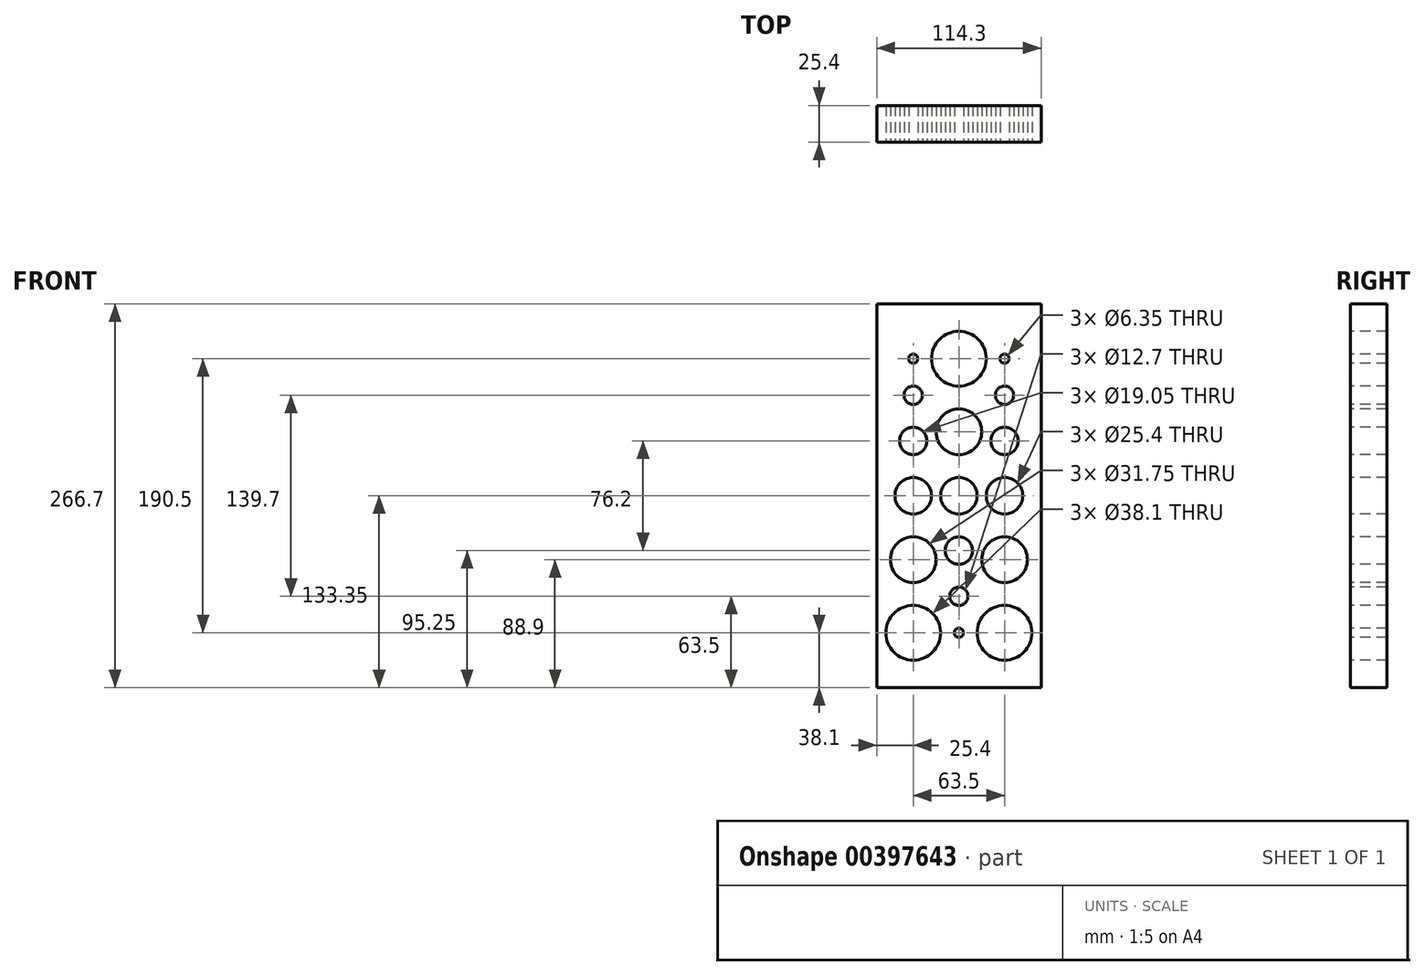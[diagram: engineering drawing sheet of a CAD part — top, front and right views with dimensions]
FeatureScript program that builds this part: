
annotation { "Feature Type Name" : "Feature", "Feature Type Description" : "" }
export const myFeature = defineFeature(function(context is Context, id is Id, definition is map)
    precondition{}
    {
        {
            var Q0;
            Q0=qCreatedBy(makeId("Front.planeOp"),FACE);
            var sketch = newSketch(context, id + "F0", { "sketchPlane" : qUnion([Q0])});
            skLineSegment(sketch, "E0.bottom", {"start": v(0, 0) * mm, "end": v(-114.3, 0) * mm});
            skLineSegment(sketch, "E0.top", {"start": v(0, 266.7) * mm, "end": v(-114.3, 266.7) * mm});
            skLineSegment(sketch, "E0.left", {"start": v(0, 0) * mm, "end": v(0, 266.7) * mm});
            skLineSegment(sketch, "E0.right", {"start": v(-114.3, 0) * mm, "end": v(-114.3, 266.7) * mm});
            skSolve(sketch);
        }
        {
            var Q0;
            Q0=qSketchRegion(id+"F0",true);
            extrude(context, id + "F1", {"entities" : qUnion([Q0]), "depth" : 25.4 * mm});
        }
        {
            var Q0;
            Q0=makeQuery(id+"F1.opExtrude","CAP_FACE",FACE,{"disambiguationData":[OSD([sQuery(id+"F0.wireOp",EDGE,"E0.bottom"),sQuery(id+"F0.wireOp",EDGE,"E0.top"),sQuery(id+"F0.wireOp",EDGE,"E0.left"),sQuery(id+"F0.wireOp",EDGE,"E0.right")])],"isStart":false});
            var sketch = newSketch(context, id + "F2", { "sketchPlane" : qUnion([Q0])});
            skLineSegment(sketch, "E1", {"start": v(0, 0) * mm, "end": v(-50.8, 0) * mm});
            skLineSegment(sketch, "E2", {"start": v(0, 0) * mm, "end": v(-25.4, 0) * mm});
            skLineSegment(sketch, "E3", {"start": v(-114.3, 0) * mm, "end": v(-63.5, 0) * mm});
            skLineSegment(sketch, "E4", {"start": v(-114.3, 0) * mm, "end": v(-88.9, 0) * mm});
            skLineSegment(sketch, "E5", {"start": v(-25.4, 0) * mm, "end": v(-25.4, 38.1) * mm});
            skCircle(sketch, "E6", {"center": v(-25.4, 38.1) * mm, "radius": 19.05 * mm});
            skLineSegment(sketch, "E7", {"start": v(-25.4, 38.1) * mm, "end": v(-25.4, 88.9) * mm});
            skLineSegment(sketch, "E8", {"start": v(-25.4, 88.9) * mm, "end": v(-25.4, 133.35) * mm});
            skLineSegment(sketch, "E9", {"start": v(-25.4, 171.45) * mm, "end": v(-25.4, 203.2) * mm});
            skLineSegment(sketch, "E10", {"start": v(-25.4, 203.2) * mm, "end": v(-25.4, 228.6) * mm});
            skLineSegment(sketch, "E11.direction1", {"start": v(-25.4, 38.1) * mm, "end": v(-88.9, 38.1) * mm, "construction": true});
            skCircle(sketch, "E12", {"center": v(-25.4, 88.9) * mm, "radius": 15.88 * mm});
            skCircle(sketch, "E13", {"center": v(-25.4, 133.35) * mm, "radius": 12.7 * mm});
            skCircle(sketch, "E14", {"center": v(-25.4, 171.45) * mm, "radius": 9.53 * mm});
            skCircle(sketch, "E15", {"center": v(-25.4, 203.2) * mm, "radius": 6.35 * mm});
            skCircle(sketch, "E16", {"center": v(-25.4, 228.6) * mm, "radius": 3.18 * mm});
            skLineSegment(sketch, "E17", {"start": v(-25.4, 171.45) * mm, "end": v(-25.4, 133.35) * mm});
            skLineSegment(sketch, "E18", {"start": v(-25.4, 228.6) * mm, "end": v(-25.4, 266.7) * mm});
            skCircle(sketch, "E19.1.0.0", {"center": v(-88.9, 228.6) * mm, "radius": 3.18 * mm});
            skCircle(sketch, "E19.1.0.1", {"center": v(-88.9, 203.2) * mm, "radius": 6.35 * mm});
            skCircle(sketch, "E19.1.0.2", {"center": v(-88.9, 171.45) * mm, "radius": 9.53 * mm});
            skCircle(sketch, "E19.1.0.3", {"center": v(-88.9, 133.35) * mm, "radius": 12.7 * mm});
            skCircle(sketch, "E19.1.0.4", {"center": v(-88.9, 88.9) * mm, "radius": 15.88 * mm});
            skCircle(sketch, "E19.1.0.5", {"center": v(-88.9, 38.1) * mm, "radius": 19.05 * mm});
            skSolve(sketch);
        }
        {
            var Q0;
            Q0=qSketchRegion(id+"F2",true);
            extrude(context, id + "F3", {"entities" : qUnion([Q0]), "operationType" : NewBodyOperationType.REMOVE, "oppositeDirection" : true, "depth" : 25.4 * mm});
        }
        {
            var Q0;
            Q0=makeQuery(id+"F1.opExtrude","CAP_FACE",FACE,{"disambiguationData":[OSD([sQuery(id+"F0.wireOp",EDGE,"E0.bottom"),sQuery(id+"F0.wireOp",EDGE,"E0.top"),sQuery(id+"F0.wireOp",EDGE,"E0.left"),sQuery(id+"F0.wireOp",EDGE,"E0.right")])],"isStart":false});
            var sketch = newSketch(context, id + "F4", { "sketchPlane" : qUnion([Q0])});
            skLineSegment(sketch, "E20", {"start": v(0, 0) * mm, "end": v(-57.15, 0) * mm});
            skLineSegment(sketch, "E21", {"start": v(-57.15, 38.1) * mm, "end": v(-57.15, 63.5) * mm});
            skLineSegment(sketch, "E22", {"start": v(-57.15, 63.5) * mm, "end": v(-57.15, 95.25) * mm});
            skLineSegment(sketch, "E23", {"start": v(-57.15, 95.25) * mm, "end": v(-57.15, 133.35) * mm});
            skLineSegment(sketch, "E24", {"start": v(-57.15, 133.35) * mm, "end": v(-57.15, 177.8) * mm});
            skLineSegment(sketch, "E25", {"start": v(-57.15, 177.8) * mm, "end": v(-57.15, 228.6) * mm});
            skLineSegment(sketch, "E26", {"start": v(-57.15, 228.6) * mm, "end": v(-57.15, 266.7) * mm});
            skCircle(sketch, "E27", {"center": v(-57.15, 228.6) * mm, "radius": 19.05 * mm});
            skCircle(sketch, "E28", {"center": v(-57.15, 177.8) * mm, "radius": 15.88 * mm});
            skCircle(sketch, "E29", {"center": v(-57.15, 133.35) * mm, "radius": 12.7 * mm});
            skCircle(sketch, "E30", {"center": v(-57.15, 95.25) * mm, "radius": 9.53 * mm});
            skCircle(sketch, "E31", {"center": v(-57.15, 63.5) * mm, "radius": 6.35 * mm});
            skCircle(sketch, "E32", {"center": v(-57.15, 38.1) * mm, "radius": 3.18 * mm});
            skSolve(sketch);
        }
        {
            var Q0;
            Q0=qSketchRegion(id+"F4",true);
            extrude(context, id + "F5", {"entities" : qUnion([Q0]), "operationType" : NewBodyOperationType.REMOVE, "oppositeDirection" : true, "depth" : 25.4 * mm});
        }
    });
